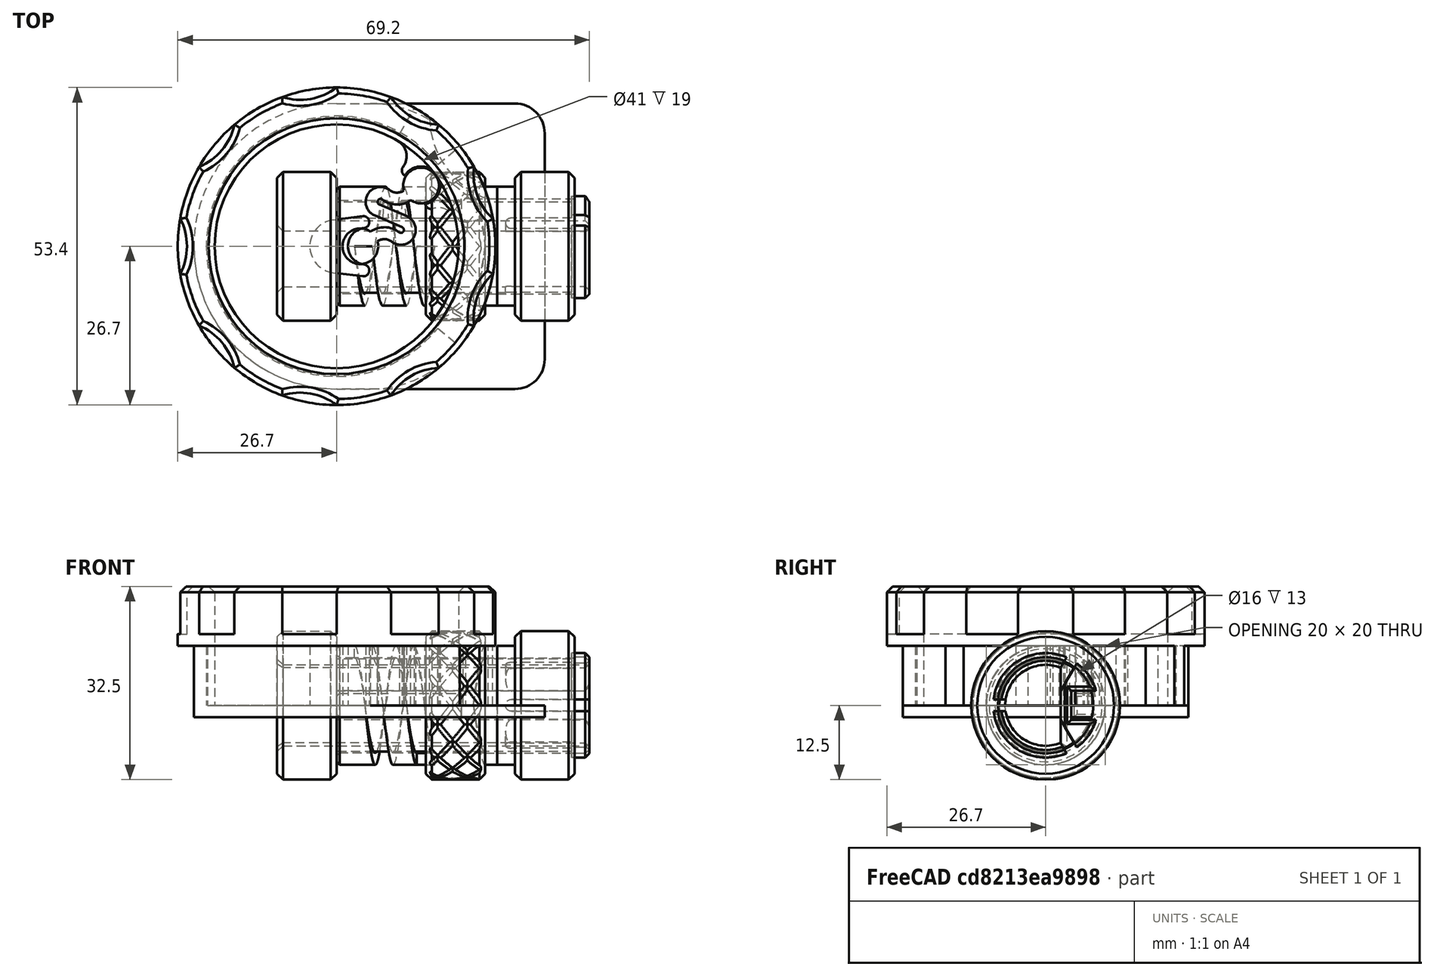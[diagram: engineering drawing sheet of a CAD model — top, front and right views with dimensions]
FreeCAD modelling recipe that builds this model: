
FCSTD DOCUMENT  (FreeCAD 1.1R20260108 (Git shallow))
Label: Compliance rotative switch v0
License: Creative Commons Attribution-NonCommercial-ShareAlike 4.0
LicenseURL: https://creativecommons.org/licenses/by-nc-sa/4.0/
objects: Sketcher::SketchObject×24, PartDesign::Pad×15, PartDesign::SubShapeBinder×13, App::Point×9, PartDesign::Chamfer×7, PartDesign::Body×6, PartDesign::Pocket×5, PartDesign::Mirrored×4, PartDesign::PolarPattern×3, PartDesign::SubtractiveHelix×3, App::Part×3, PartDesign::MultiTransform×2
note: 175 computed .brp shape members not serialized (recipe doc carries the construction recipe); baked Part::Feature solids carry a one-line shape summary decoded from their .brp

FEATURE [App::Point] Origin001  label="Origine"
  Role = Origin
FEATURE [Sketcher::SketchObject] Sketch
  ArcFitTolerance = 1e-06
  AttachmentSupport = -> [Origin]
  ExternalTypes = [0]
  FullyConstrained = true
  MakeInternals = false
  MapMode = 5
  sketch-geometry (19):
    g0: Circle [constr] CenterX=0 CenterY=0 CenterZ=0 NormalX=0 NormalY=0 NormalZ=1 AngleXU=0 Radius=17.5
    g1: ArcOfCircle CenterX=4 CenterY=0 CenterZ=0 NormalX=0 NormalY=0 NormalZ=1 AngleXU=0 Radius=3 StartAngle=0.958197 EndAngle=6.56171
    g2: ArcOfCircle CenterX=14.2117 CenterY=10.2117 CenterZ=0 NormalX=0 NormalY=0 NormalZ=1 AngleXU=0 Radius=3 StartAngle=4.09979 EndAngle=9.7033
    g3: ArcOfCircle CenterX=10.1679 CenterY=11.0165 CenterZ=0 NormalX=0 NormalY=0 NormalZ=1 AngleXU=0 Radius=4 StartAngle=4.04957 EndAngle=5.33075
    g4: LineSegment [constr] StartX=4 StartY=0 StartZ=0 EndX=6.30469 EndY=1.63964 EndZ=0
    g5: LineSegment [constr] StartX=5.72499 StartY=2.45447 StartZ=0 EndX=6.88439 EndY=0.824807 EndZ=0
    g6: LineSegment [constr] StartX=11.3273 StartY=9.38687 StartZ=0 EndX=12.4867 EndY=7.75721 EndZ=0
    g7: LineSegment [constr] StartX=11.907 StartY=8.57204 StartZ=0 EndX=14.2117 EndY=10.2117 EndZ=0
    g8: ArcOfCircle CenterX=10.1679 CenterY=11.0165 CenterZ=0 NormalX=0 NormalY=0 NormalZ=1 AngleXU=0 Radius=2 StartAngle=4.04957 EndAngle=5.33075
    g9: LineSegment [constr] StartX=4 StartY=0 StartZ=0 EndX=14.2117 EndY=10.2117 EndZ=0
    g10: ArcOfCircle CenterX=8.04379 CenterY=-0.804853 CenterZ=0 NormalX=0 NormalY=0 NormalZ=1 AngleXU=0 Radius=2 StartAngle=0.907978 EndAngle=2.18916
    g11: ArcOfCircle CenterX=8.04379 CenterY=-0.804853 CenterZ=0 NormalX=0 NormalY=0 NormalZ=1 AngleXU=0 Radius=4 StartAngle=0.907978 EndAngle=2.18916
    g12: Circle [constr] CenterX=9.10584 CenterY=5.10584 CenterZ=0 NormalX=0 NormalY=0 NormalZ=1 AngleXU=0 Radius=1
    g13: LineSegment StartX=6.41406 StartY=5.17149 StartZ=0 EndX=11.0098 EndY=3.20189 EndZ=0
    g14: LineSegment StartX=7.20189 StartY=7.00978 StartZ=0 EndX=11.7976 EndY=5.04018 EndZ=0
    g15: ArcOfCircle CenterX=10.8128 CenterY=2.74232 CenterZ=0 NormalX=0 NormalY=0 NormalZ=1 AngleXU=0 Radius=0.5 StartAngle=4.04957 EndAngle=7.44909
    g16: ArcOfCircle CenterX=10.8128 CenterY=2.74232 CenterZ=0 NormalX=0 NormalY=0 NormalZ=1 AngleXU=0 Radius=2.5 StartAngle=4.04957 EndAngle=7.44909
    g17: ArcOfCircle CenterX=7.39885 CenterY=7.46935 CenterZ=0 NormalX=0 NormalY=0 NormalZ=1 AngleXU=0 Radius=0.5 StartAngle=0.907978 EndAngle=4.3075
    g18: ArcOfCircle CenterX=7.39885 CenterY=7.46935 CenterZ=0 NormalX=0 NormalY=0 NormalZ=1 AngleXU=0 Radius=2.5 StartAngle=0.907978 EndAngle=4.3075
  constraints (49):
    c: Coincident(g0,g-1)
    c: Equal(g1,g2)
    c: Radius(g2) = 3
    c: Diameter(g0) = 35
    c: Coincident(g3,g2)
    c: Coincident(g5,g1)
    c: Coincident(g5,g1)
    c: Perpendicular(g4,g5)
    c: Coincident(g6,g2)
    c: Coincident(g6,g2)
    c: Symmetric(g6,g6,g7)
    c: Coincident(g7,g2)
    c: Perpendicular(g3,g6)
    c: Coincident(g8,g2)
    c: Distance(g5,g5) = 2
    c: Coincident(g9,g2)
    c: PointOnObject(g4,g5)
    c: Coincident(g10,g1)
    c: Coincident(g11,g10)
    c: Coincident(g11,g1)
    c: Perpendicular(g10,g5)
    c: Coincident(g3,g8)
    c: Symmetric(g9,g9,g12)
    c: Coincident(g9,g1)
    c: Coincident(g1,g4)
    c: Radius(g10) = 2
    c: Equal(g3,g11)
    c: Distance(g1,g0) = 4
    c: PointOnObject(g2,g0)
    c: PointOnObject(g1,g-1)
    c: Angle(g-1,g9) = 0.785398
    c: Tangent(g13,g12)
    c: Tangent(g14,g12)
    c: Coincident(g15,g13)
    c: Coincident(g16,g15)
    c: Coincident(g18,g17)
    c: Tangent(g13,g15,g13) = 1.5708
    c: Tangent(g15,g11) = 1.5708
    c: Tangent(g16,g10) = 1.5708
    c: Tangent(g18,g13) = -1.5708
    c: Tangent(g17,g14) = -1.5708
    c: Tangent(g17,g3) = 1.5708
    c: Tangent(g18,g8) = 1.5708
    c: Tangent(g16,g14) = 1.5708
    c: Equal(g16,g18)
    c: Equal(g17,g15)
    c: Radius(g15) = 0.5
    c: Symmetric(g13,g14,g9)
    c: Distance(g13,g13) = 5
FEATURE [App::Point] Origin003  label="Origine002"
  Role = Origin
FEATURE [PartDesign::SubShapeBinder] Binder
  BindCopyOnChange = 0
  BindMode = 0
  ClaimChildren = false
  Context = -> Body001 [Binder.]
  Fuse = false
  MakeFace = true
  OffsetFill = false
  OffsetIntersection = false
  OffsetJoinType = 0
  OffsetOpenResult = false
  PartialLoad = false
  Refine = true
  Relative = true
  Support = -> [Body[Sketch.Edge1]]
  _Version = 2
FEATURE [PartDesign::SubShapeBinder] Binder001
  BindCopyOnChange = 0
  BindMode = 0
  ClaimChildren = false
  Context = -> Body001 [Binder001.]
  Fuse = false
  MakeFace = true
  OffsetFill = false
  OffsetIntersection = false
  OffsetJoinType = 0
  OffsetOpenResult = false
  PartialLoad = false
  Refine = true
  Relative = true
  Support = -> [Body[Pad.]]
  _Version = 2
FEATURE [Sketcher::SketchObject] Sketch001
  ArcFitTolerance = 1e-06
  AttachmentSupport = -> [Origin002]
  ExternalTypes = [0,0]
  FullyConstrained = false
  MakeInternals = false
  MapMode = 5
  sketch-geometry (10):
    g0: Circle CenterX=0 CenterY=0 CenterZ=0 NormalX=0 NormalY=0 NormalZ=1 AngleXU=0 Radius=21.7
    g1: ArcOfCircle CenterX=0 CenterY=0 CenterZ=0 NormalX=0 NormalY=0 NormalZ=1 AngleXU=0 Radius=20.5 StartAngle=1.04586 EndAngle=6.48345
    g2: ArcOfCircle CenterX=15.9013 CenterY=7.30734 CenterZ=0 NormalX=0 NormalY=0 NormalZ=1 AngleXU=0 Radius=1.02476 StartAngle=3.35859 EndAngle=5.0279
    g3: LineSegment [constr] StartX=14.9006 StartY=7.08672 StartZ=0 EndX=14.2117 EndY=10.2117 EndZ=0
    g4: ArcOfCircle CenterX=11.9981 CenterY=12.7395 CenterZ=0 NormalX=0 NormalY=0 NormalZ=1 AngleXU=0 Radius=1.02476 StartAngle=2.50141 EndAngle=4.17072
    g5: ArcOfCircle CenterX=8.77029 CenterY=15.1437 CenterZ=0 NormalX=0 NormalY=0 NormalZ=1 AngleXU=0 Radius=3 StartAngle=5.643 EndAngle=7.32904
    g6: LineSegment [constr] StartX=11.4698 StartY=11.8615 StartZ=0 EndX=14.2117 EndY=10.2117 EndZ=0
    g7: LineSegment [constr] StartX=13.1691 StartY=9.46257 StartZ=0 EndX=0 EndY=0 EndZ=0
    g8: ArcOfCircle CenterX=17.1502 CenterY=3.48126 CenterZ=0 NormalX=0 NormalY=0 NormalZ=1 AngleXU=0 Radius=3 StartAngle=0.200265 EndAngle=1.88631
    g9: ArcOfCircle CenterX=14.2117 CenterY=10.2117 CenterZ=0 NormalX=0 NormalY=0 NormalZ=1 AngleXU=0 Radius=3.2 StartAngle=4.92938 EndAngle=8.88311
  constraints (23):
    c: Coincident(g0,g-1)
    c: Coincident(g1,g0)
    c: Tangent(g1,g-3)
    c: Distance(g1,g0) = 1.2
    c: Distance(g2,g-4) = 1
    c: Coincident(g3,g-3)
    c: Tangent(g3,g2) = 1.5708
    c: Equal(g2,g4)
    c: Tangent(g5,g4) = 1.5708
    c: Tangent(g5,g1) = -1.5708
    c: Coincident(g6,g3)
    c: Tangent(g6,g4) = -1.5708
    c: Coincident(g7,g0)
    c: Symmetric(g2,g4,g7)
    c: Tangent(g8,g1) = -1.5708
    c: Tangent(g8,g2) = 1.5708
    c: Equal(g8,g5)
    c: PointOnObject(g8,g-4)
    c: PointOnObject(g4,g-4)
    c: Coincident(g9,g3)
    c: Distance(g9,g-3) = 0.2
    c: Coincident(g9,g2)
    c: Coincident(g9,g4)
FEATURE [PartDesign::Pad] Pad001
  Direction = (0,0,1)
  Length = 10
  Length2 = 10
  Profile = -> Sketch001
  ReferenceAxis = -> Sketch001 [N_Axis]
  Refine = true
  SideType = 0
  Suppressed = false
  Type = 0
  Type2 = 0
FEATURE [App::Point] Origin005  label="Origine004"
  Role = Origin
FEATURE [PartDesign::SubShapeBinder] Binder002
  BindCopyOnChange = 0
  BindMode = 0
  ClaimChildren = false
  Context = -> Body002 [Binder002.]
  Fuse = false
  MakeFace = true
  OffsetFill = false
  OffsetIntersection = false
  OffsetJoinType = 0
  OffsetOpenResult = false
  PartialLoad = false
  Refine = true
  Relative = true
  Support = -> [Body001]
  _Version = 2
FEATURE [PartDesign::SubShapeBinder] Binder003
  BindCopyOnChange = 0
  BindMode = 0
  ClaimChildren = false
  Context = -> Body002 [Binder003.]
  Fuse = false
  MakeFace = true
  OffsetFill = false
  OffsetIntersection = false
  OffsetJoinType = 0
  OffsetOpenResult = false
  PartialLoad = false
  Refine = true
  Relative = true
  Support = -> [Body]
  _Version = 2
FEATURE [Sketcher::SketchObject] Sketch002  label="Master"
  ArcFitTolerance = 1e-06
  AttachmentSupport = -> [Origin004]
  ExternalTypes = [0,0,0]
  FullyConstrained = true
  MakeInternals = false
  MapMode = 5
  sketch-geometry (13):
    g0: LineSegment StartX=1.5e-15 StartY=24 StartZ=0 EndX=30 EndY=24 EndZ=0
    g1: LineSegment StartX=35 StartY=19 StartZ=0 EndX=35 EndY=-19 EndZ=0
    g2: LineSegment StartX=30 StartY=-24 StartZ=0 EndX=-3.6e-15 EndY=-24 EndZ=0
    g3: ArcOfCircle CenterX=0 CenterY=0 CenterZ=0 NormalX=0 NormalY=0 NormalZ=1 AngleXU=0 Radius=24 StartAngle=1.5708 EndAngle=4.71239
    g4: ArcOfCircle CenterX=4 CenterY=0 CenterZ=0 NormalX=0 NormalY=0 NormalZ=1 AngleXU=0 Radius=5.2 StartAngle=1.8112 EndAngle=4.47198
    g5: ArcOfCircle CenterX=3 CenterY=4.07922 CenterZ=0 NormalX=0 NormalY=0 NormalZ=1 AngleXU=0 Radius=1 StartAngle=4.95279 EndAngle=8.09439
    g6: ArcOfCircle CenterX=3 CenterY=-4.07922 CenterZ=0 NormalX=0 NormalY=0 NormalZ=1 AngleXU=0 Radius=1 StartAngle=4.47198 EndAngle=7.61358
    g7: ArcOfCircle CenterX=4 CenterY=0 CenterZ=0 NormalX=0 NormalY=0 NormalZ=1 AngleXU=0 Radius=3.2 StartAngle=1.8112 EndAngle=4.47198
    g8: ArcOfCircle CenterX=30 CenterY=19 CenterZ=0 NormalX=0 NormalY=0 NormalZ=1 AngleXU=0 Radius=5 StartAngle=0 EndAngle=1.5708
    g9: GeomPoint [constr] X=35 Y=24 Z=0
    g10: ArcOfCircle CenterX=30 CenterY=-19 CenterZ=0 NormalX=0 NormalY=0 NormalZ=1 AngleXU=0 Radius=5 StartAngle=4.71239 EndAngle=6.28319
    g11: GeomPoint [constr] X=35 Y=-24 Z=0
    g12: LineSegment [constr] StartX=4 StartY=4.07922 StartZ=0 EndX=4 EndY=-4.07922 EndZ=0
  constraints (32):
    c: PointOnObject(g0,g-2)
    c: Horizontal(g0)
    c: Vertical(g1)
    c: PointOnObject(g2,g-2)
    c: Tangent(g2,g3) = 1.5708
    c: Coincident(g3,g0)
    c: Coincident(g3,g-1)
    c: Radius(g3) = 24
    c: Coincident(g4,g7)
    c: Tangent(g7,g6) = 1.5708
    c: Tangent(g7,g5) = 1.5708
    c: Tangent(g4,g6) = -1.5708
    c: Tangent(g4,g5) = -1.5708
    c: Radius(g6) = 1
    c: Coincident(g4,g-4)
    c: Distance(g6,g-4) = 0.2
    c: Vertical(g6,g5)
    c: DistanceX(g2,g11) = 35
    c: PointOnObject(g9,g0)
    c: PointOnObject(g9,g1)
    c: Tangent(g0,g8) = 1.5708
    c: Tangent(g1,g8) = 1.5708
    c: PointOnObject(g11,g2)
    c: PointOnObject(g11,g1)
    c: Tangent(g2,g10) = 1.5708
    c: Tangent(g1,g10) = 1.5708
    c: Equal(g10,g8)
    c: Radius(g8) = 5
    c: PointOnObject(g12,g5)
    c: Tangent(g12,g6) = 1.5708
    c: Vertical(g12)
    c: PointOnObject(g4,g12)
FEATURE [Sketcher::SketchObject] Sketch004
  ArcFitTolerance = 1e-06
  AttachmentSupport = -> [Origin002]
  ExternalGeometry = -> [Pad001]
  ExternalTypes = [0,0]
  FullyConstrained = true
  MakeInternals = false
  MapMode = 5
  sketch-geometry (7):
    g0: LineSegment StartX=21.3184 StartY=4.05156 StartZ=0 EndX=26.2305 EndY=4.9851 EndZ=0
    g1: LineSegment StartX=10.6404 StartY=18.9122 StartZ=0 EndX=13.0921 EndY=23.2698 EndZ=0
    g2: ArcOfCircle CenterX=0 CenterY=0 CenterZ=0 NormalX=0 NormalY=0 NormalZ=1 AngleXU=0 Radius=26.7 StartAngle=0.18781 EndAngle=0.300229
    g3: ArcOfCircle CenterX=30.616 CenterY=21.9989 CenterZ=0 NormalX=0 NormalY=0 NormalZ=1 AngleXU=0 Radius=15 StartAngle=3.16457 EndAngle=4.36474
    g4: ArcOfCircle CenterX=0 CenterY=0 CenterZ=0 NormalX=0 NormalY=0 NormalZ=1 AngleXU=0 Radius=26.7 StartAngle=0.945895 EndAngle=1.05831
    g5: ArcOfCircle CenterX=0 CenterY=0 CenterZ=0 NormalX=0 NormalY=0 NormalZ=1 AngleXU=0 Radius=21.7 StartAngle=0.18781 EndAngle=1.05831
    g6: LineSegment [constr] StartX=0 StartY=0 StartZ=0 EndX=18.4346 EndY=13.246 EndZ=0
  constraints (21):
    c: PointOnObject(g-1,g1)
    c: Distance(g1,g1) = 5
    c: PointOnObject(g-1,g0)
    c: Coincident(g2,g-1)
    c: Coincident(g4,g1)
    c: Coincident(g2,g0)
    c: Radius(g3) = 15
    c: Distance(g3,g-4) = 1
    c: Coincident(g3,g4)
    c: Coincident(g3,g2)
    c: Coincident(g2,g4)
    c: Coincident(g0,g5)
    c: Coincident(g5,g2)
    c: Coincident(g1,g5)
    c: PointOnObject(g1,g-4)
    c: Coincident(g6,g2)
    c: Symmetric(g0,g1,g6)
    c: PointOnObject(g3,g6)
    c: PointOnObject(g-3,g6)
    c: Distance(g0,g2) = 3
    c: PointOnObject(g6,g3)
FEATURE [PartDesign::Pad] Pad005
  BaseFeature = -> Pad001
  Direction = (0,0,1)
  Length = 15
  Length2 = -5
  Profile = -> Sketch004
  ReferenceAxis = -> Sketch004 [N_Axis]
  Refine = true
  SideType = 0
  Suppressed = false
  Type = 3
  Type2 = 0
  UpToFace = -> Pad001 [Face9]
FEATURE [Sketcher::SketchObject] Sketch005
  ArcFitTolerance = 1e-06
  ExternalGeometry = -> [Binder002]
  ExternalTypes = [0,0]
  FullyConstrained = true
  MakeInternals = false
  MapMode = 5
  sketch-geometry (7):
    g0: LineSegment StartX=1.5e-15 StartY=24 StartZ=0 EndX=5.66707 EndY=24 EndZ=0
    g1: ArcOfCircle CenterX=0 CenterY=0 CenterZ=0 NormalX=0 NormalY=0 NormalZ=1 AngleXU=0 Radius=24 StartAngle=1.5708 EndAngle=3.14159
    g2: LineSegment StartX=-24 StartY=2.9e-15 StartZ=0 EndX=-21.9 EndY=2.9e-15 EndZ=0
    g3: ArcOfCircle CenterX=0 CenterY=0 CenterZ=0 NormalX=0 NormalY=0 NormalZ=1 AngleXU=0 Radius=21.9 StartAngle=0.681557 EndAngle=3.14159
    g4: LineSegment StartX=17.0074 StartY=13.7971 StartZ=0 EndX=20.735 EndY=16.8211 EndZ=0
    g5: ArcOfCircle CenterX=5.66707 CenterY=4.59734 CenterZ=0 NormalX=0 NormalY=0 NormalZ=1 AngleXU=0 Radius=19.4027 StartAngle=0.681558 EndAngle=1.5708
    g6: ArcOfCircle [constr] CenterX=0 CenterY=0 CenterZ=0 NormalX=0 NormalY=0 NormalZ=1 AngleXU=0 Radius=26.7 StartAngle=0.681557 EndAngle=1.05831
  constraints (19):
    c: PointOnObject(g0,g-6)
    c: Coincident(g1,g-6)
    c: PointOnObject(g1,g-1)
    c: Coincident(g2,g1)
    c: Horizontal(g2)
    c: Coincident(g-6,g0)
    c: Coincident(g1,g-3)
    c: Coincident(g3,g1)
    c: Coincident(g3,g2)
    c: Distance(g2,g-7) = 0.2
    c: Coincident(g4,g3)
    c: PointOnObject(g1,g4)
    c: Distance(g-8,g4) = 10
    c: Coincident(g5,g4)
    c: Tangent(g5,g0) = 1.5708
    c: Coincident(g6,g1)
    c: Coincident(g6,g-8)
    c: Coincident(g6,g4)
    c: Tangent(g6,g5)
FEATURE [Sketcher::SketchObject] Sketch006
  ArcFitTolerance = 1e-06
  AttachmentSupport = -> [Pad005]
  ExternalGeometry = -> [Pad005]
  ExternalTypes = [0,0]
  FullyConstrained = true
  MakeInternals = false
  MapMode = 5
  Placement = pos=(0,0,10) rot=(0,0,1;0rad)
  sketch-geometry (2):
    g0: Circle CenterX=0 CenterY=0 CenterZ=0 NormalX=0 NormalY=0 NormalZ=1 AngleXU=0 Radius=20.5
    g1: Circle CenterX=0 CenterY=0 CenterZ=0 NormalX=0 NormalY=0 NormalZ=1 AngleXU=0 Radius=26.7
  constraints (4):
    c: Coincident(g0,g-1)
    c: PointOnObject(g-4,g0)
    c: Coincident(g1,g0)
    c: PointOnObject(g-3,g1)
FEATURE [PartDesign::Pad] Pad007
  BaseFeature = -> Pad005
  Direction = (0,0,1)
  Length = 10
  Length2 = 10
  Profile = -> Sketch006
  ReferenceAxis = -> Sketch006 [N_Axis]
  Refine = true
  SideType = 0
  Suppressed = false
  Type = 0
  Type2 = 0
FEATURE [Sketcher::SketchObject] Sketch007
  ArcFitTolerance = 1e-06
  AttachmentSupport = -> [Pad007]
  ExternalGeometry = -> [Pad007]
  ExternalTypes = [0]
  FullyConstrained = false
  MakeInternals = false
  MapMode = 5
  Placement = pos=(0,0,20) rot=(0,0,1;0rad)
  sketch-geometry (5):
    g0: ArcOfCircle CenterX=-35.1546 CenterY=1.9e-15 CenterZ=0 NormalX=0 NormalY=0 NormalZ=1 AngleXU=0 Radius=10 StartAngle=5.80109 EndAngle=6.76529
    g1: LineSegment [constr] StartX=-26.2944 StartY=4.63641 StartZ=0 EndX=0 EndY=0 EndZ=0
    g2: LineSegment [constr] StartX=-26.2944 StartY=-4.63641 StartZ=0 EndX=0 EndY=0 EndZ=0
    g3: LineSegment [constr] StartX=-26.2944 StartY=4.63641 StartZ=0 EndX=-26.2944 EndY=-4.63641 EndZ=0
    g4: ArcOfCircle CenterX=0 CenterY=0 CenterZ=0 NormalX=0 NormalY=0 NormalZ=1 AngleXU=0 Radius=26.7 StartAngle=2.96706 EndAngle=3.31613
  constraints (13):
    c: Symmetric(g0,g0,g-1)
    c: Coincident(g1,g0)
    c: Coincident(g1,g-1)
    c: Coincident(g2,g0)
    c: Radius(g0) = 10
    c: Coincident(g2,g1)
    c: Coincident(g3,g0)
    c: Coincident(g3,g0)
    c: Coincident(g4,g0)
    c: Coincident(g4,g1)
    c: PointOnObject(g4,g-3)
    c: Horizontal(g0,g4)
    c: Angle(g1,g2) = 0.349066
FEATURE [PartDesign::Pocket] Pocket
  BaseFeature = -> Pad007
  Direction = (0,0,-1)
  Length = 8
  Length2 = 5
  Profile = -> Sketch007
  ReferenceAxis = -> Sketch007 [N_Axis]
  Refine = true
  SideType = 0
  Suppressed = false
  Type = 0
  Type2 = 0
FEATURE [PartDesign::PolarPattern] PolarPattern
  Angle = 360
  Axis = -> Sketch007 [N_Axis]
  BaseFeature = -> Pocket
  Mode = 0
  Occurrences = 9
  Offset = 120
  Originals = -> [Pocket]
  Refine = true
  SpacingPattern = [0]
  Spacings = [-1,-1,-1,-1,-1,-1,-1,-1]
  Suppressed = false
  TransformMode = 0
FEATURE [PartDesign::Chamfer] Chamfer
  Angle = 45
  Base = -> PolarPattern [Face14]
  BaseFeature = -> PolarPattern
  ChamferType = 0
  FlipDirection = false
  Refine = true
  Size = 1
  Size2 = 1
  SupportTransform = false
  Suppressed = false
  UseAllEdges = false
FEATURE [PartDesign::Body] Body001  label="Bouton"
  AllowCompound = false
  Group = -> [Binder,Binder001,Sketch001,Pad001,Sketch004,Pad005,Pad007,Pocket,Sketch006,Sketch007,PolarPattern,Chamfer]
  Origin = -> Origin002
  Tip = -> Chamfer
FEATURE [Sketcher::SketchObject] Sketch008
  ArcFitTolerance = 1e-06
  AttachmentSupport = -> [Origin004]
  ExternalGeometry = -> [Sketch002]
  ExternalTypes = [0,0,0,0,0,0]
  FullyConstrained = true
  MakeInternals = false
  MapMode = 5
FEATURE [PartDesign::Pad] Pad008  label="Plaque"
  Direction = (0,0,1)
  Length = 2
  Length2 = 10
  Profile = -> Sketch008
  ReferenceAxis = -> Sketch008 [N_Axis]
  Refine = true
  Reversed = true
  SideType = 0
  Suppressed = false
  Type = 0
  Type2 = 0
FEATURE [Sketcher::SketchObject] Sketch009  label="Axis"
  ArcFitTolerance = 1e-06
  AttachmentSupport = -> [Origin004]
  ExternalGeometry = -> [Sketch002]
  ExternalTypes = [0,0,0,0]
  FullyConstrained = true
  MakeInternals = false
  MapMode = 5
  sketch-geometry (7):
    g0: ArcOfCircle [constr] CenterX=5 CenterY=0 CenterZ=0 NormalX=0 NormalY=0 NormalZ=1 AngleXU=0 Radius=5.08839 StartAngle=1.69297 EndAngle=4.59022
    g1: ArcOfCircle CenterX=4.50175 CenterY=4.05791 CenterZ=0 NormalX=0 NormalY=0 NormalZ=1 AngleXU=0 Radius=1 StartAngle=4.83456 EndAngle=7.97615
    g2: ArcOfCircle CenterX=4.50175 CenterY=-4.05791 CenterZ=0 NormalX=0 NormalY=0 NormalZ=1 AngleXU=0 Radius=1 StartAngle=4.59022 EndAngle=7.73181
    g3: ArcOfCircle CenterX=5 CenterY=0 CenterZ=0 NormalX=0 NormalY=0 NormalZ=1 AngleXU=0 Radius=3.08839 StartAngle=1.69297 EndAngle=4.59022
    g4: ArcOfCircle CenterX=0 CenterY=0 CenterZ=0 NormalX=0 NormalY=0 NormalZ=1 AngleXU=0 Radius=4.47904 StartAngle=1.69297 EndAngle=4.59022
    g5: LineSegment StartX=-0.545858 StartY=4.44565 StartZ=0 EndX=4.37988 EndY=5.05046 EndZ=0
    g6: LineSegment StartX=-0.545858 StartY=-4.44565 StartZ=0 EndX=4.37988 EndY=-5.05046 EndZ=0
  constraints (16):
    c: Coincident(g0,g3)
    c: Tangent(g3,g2) = 1.5708
    c: Tangent(g3,g1) = 1.5708
    c: Tangent(g0,g2) = -1.5708
    c: Tangent(g0,g1) = -1.5708
    c: PointOnObject(g0,g-1)
    c: Equal(g1,g-4)
    c: Distance(g-5,g0) = 1
    c: Horizontal(g0,g-4)
    c: Vertical(g2,g1)
    c: Tangent(g5,g0) = 1.5708
    c: Coincident(g6,g0)
    c: Tangent(g5,g4) = 1.5708
    c: Tangent(g6,g4) = -1.5708
    c: Coincident(g4,g-1)
    c: Angle(g-1,g5) = 0.122173
FEATURE [PartDesign::Pad] Pad009  label="Axe"
  BaseFeature = -> Pad008
  Direction = (0,0,1)
  Length = 10
  Length2 = 10
  Profile = -> Sketch009
  ReferenceAxis = -> Sketch009 [N_Axis]
  Refine = true
  SideType = 0
  Suppressed = false
  Type = 3
  Type2 = 0
  UpToFace = -> Binder003 [Face14]
FEATURE [PartDesign::Pad] Pad006
  BaseFeature = -> Pad009
  Direction = (0,0,1)
  Length = 10
  Length2 = 10
  Profile = -> Sketch005
  ReferenceAxis = -> Sketch005 [N_Axis]
  Refine = true
  SideType = 0
  Suppressed = false
  Type = 3
  Type2 = 0
  UpToFace = -> Binder002 [Face3]
FEATURE [PartDesign::Mirrored] Mirrored
  BaseFeature = -> Pad006
  MirrorPlane = -> XZ_Plane002
  Originals = -> [Pad006]
  Refine = true
  Suppressed = false
  TransformMode = 0
FEATURE [PartDesign::Body] Body002  label="Support"
  AllowCompound = false
  Group = -> [Binder003,Binder002,Sketch002,Pad008,Pad009,Sketch005,Pad006,Mirrored,Sketch008,Sketch009]
  Origin = -> Origin004
  Tip = -> Mirrored
FEATURE [PartDesign::Pad] Pad
  Direction = (0,0,1)
  Length = 10
  Length2 = 10
  Profile = -> Sketch
  ReferenceAxis = -> Sketch [N_Axis]
  Refine = true
  SideType = 0
  Suppressed = false
  Type = 0
  Type2 = 0
FEATURE [PartDesign::Body] Body  label="Ressort"
  AllowCompound = false
  Group = -> [Sketch,Pad]
  Origin = -> Origin
  Tip = -> Pad
FEATURE [App::Point] Origin007  label="Origine006"
  Role = Origin
FEATURE [Sketcher::SketchObject] Sketch010
  ArcFitTolerance = 1e-06
  AttachmentSupport = -> [Origin006]
  ExternalTypes = [0]
  FullyConstrained = true
  MakeInternals = false
  MapMode = 5
  Placement = pos=(0,0,0) rot=(0.57735,0.57735,0.57735;2.0944rad)
  sketch-geometry (5):
    g0: Circle CenterX=0 CenterY=0 CenterZ=0 NormalX=0 NormalY=0 NormalZ=1 AngleXU=0 Radius=10
    g1: ArcOfCircle CenterX=0 CenterY=0 CenterZ=0 NormalX=0 NormalY=0 NormalZ=1 AngleXU=0 Radius=8 StartAngle=0.25268 EndAngle=6.03051
    g2: LineSegment StartX=7.74597 StartY=2 StartZ=0 EndX=4.74597 EndY=2 EndZ=0
    g3: LineSegment StartX=4.74597 StartY=2 StartZ=0 EndX=4.74597 EndY=-2 EndZ=0
    g4: LineSegment StartX=4.74597 StartY=-2 StartZ=0 EndX=7.74597 EndY=-2 EndZ=0
  constraints (13):
    c: Diameter(g0) = 20
    c: Coincident(g0,g-1)
    c: Coincident(g1,g0)
    c: Coincident(g2,g3)
    c: Coincident(g3,g4)
    c: Distance(g3,g3) = 4
    c: Distance(g4,g4) = 3
    c: Distance(g0,g1) = 2
    c: Coincident(g2,g1)
    c: Coincident(g4,g1)
    c: Horizontal(g4)
    c: Horizontal(g2)
    c: Symmetric(g2,g3,g-1)
FEATURE [PartDesign::Pad] Pad010
  Direction = (1,0,0)
  Length = 25
  Length2 = 10
  Profile = -> Sketch010
  ReferenceAxis = -> Sketch010 [N_Axis]
  Refine = true
  SideType = 0
  Suppressed = false
  Type = 0
  Type2 = 0
FEATURE [Sketcher::SketchObject] Sketch011
  ArcFitTolerance = 1e-06
  AttachmentSupport = -> [Origin006]
  ExternalGeometry = -> [Pad010]
  ExternalTypes = [1,1]
  FullyConstrained = true
  MakeInternals = false
  MapMode = 5
  Placement = pos=(0,0,0) rot=(1,0,0;1.5708rad)
  sketch-geometry (4):
    g0: LineSegment StartX=6 StartY=10 StartZ=0 EndX=3 EndY=10 EndZ=0
    g1: LineSegment StartX=3 StartY=10 StartZ=0 EndX=3 EndY=0 EndZ=0
    g2: LineSegment StartX=3 StartY=0 StartZ=0 EndX=6 EndY=0 EndZ=0
    g3: LineSegment StartX=6 StartY=0 StartZ=0 EndX=6 EndY=10 EndZ=0
  constraints (12):
    c: Horizontal(g0)
    c: Horizontal(g-5,g0)
    c: DistanceX(g-5,g0) = 3
    c: Coincident(g0,g1)
    c: PointOnObject(g1,g-1)
    c: Vertical(g1)
    c: Coincident(g1,g2)
    c: Horizontal(g2)
    c: Coincident(g2,g3)
    c: Coincident(g3,g0)
    c: Vertical(g3)
    c: Distance(g0,g0) = 3
FEATURE [PartDesign::SubtractiveHelix] SubtractiveHelix
  Angle = 0
  Axis = (1,0,0)
  Base = (0,0,0)
  BaseFeature = -> Pad010
  Growth = 0
  HasBeenEdited = true
  Height = 10.5
  LeftHanded = false
  Mode = 1
  Outside = false
  Pitch = 7
  Profile = -> Sketch011
  ReferenceAxis = -> Sketch011 [H_Axis]
  Refine = true
  Suppressed = false
  Tolerance = 0.1
  Turns = 1.5
FEATURE [App::Point] Origin009  label="Origine008"
  Role = Origin
FEATURE [PartDesign::SubShapeBinder] Binder004
  BindCopyOnChange = 0
  BindMode = 0
  ClaimChildren = false
  Context = -> Part001 [Body004.Binder004.]
  Fuse = false
  MakeFace = true
  OffsetFill = false
  OffsetIntersection = false
  OffsetJoinType = 0
  OffsetOpenResult = false
  PartialLoad = false
  Refine = true
  Relative = true
  Support = -> [Body003]
  _Version = 2
FEATURE [Sketcher::SketchObject] Sketch013
  ArcFitTolerance = 1e-06
  AttachmentOffset = pos=(0,0,40) rot=(0,0,1;0rad)
  AttachmentSupport = -> [Origin008]
  ExternalTypes = [0,0]
  FullyConstrained = true
  MakeInternals = false
  MapMode = 5
  Placement = pos=(40,0,0) rot=(0.57735,0.57735,0.57735;2.0944rad)
  sketch-geometry (2):
    g0: Circle CenterX=0 CenterY=0 CenterZ=0 NormalX=0 NormalY=0 NormalZ=1 AngleXU=0 Radius=10
    g1: Circle CenterX=0 CenterY=0 CenterZ=0 NormalX=0 NormalY=0 NormalZ=1 AngleXU=0 Radius=8
  constraints (4):
    c: Coincident(g0,g-1)
    c: PointOnObject(g-3,g0)
    c: Coincident(g1,g0)
    c: PointOnObject(g-4,g1)
FEATURE [App::Point] Origin011  label="Origine010"
  Role = Origin
FEATURE [PartDesign::SubShapeBinder] Binder005
  BindCopyOnChange = 0
  BindMode = 0
  ClaimChildren = false
  Context = -> Part001 [Body005.Binder005.]
  Fuse = false
  MakeFace = true
  OffsetFill = false
  OffsetIntersection = false
  OffsetJoinType = 0
  OffsetOpenResult = false
  PartialLoad = false
  Refine = true
  Relative = true
  Support = -> [Body003]
  _Version = 2
FEATURE [PartDesign::SubShapeBinder] Binder006
  BindCopyOnChange = 0
  BindMode = 0
  ClaimChildren = false
  Context = -> Part001 [Body005.Binder006.]
  Fuse = false
  MakeFace = true
  OffsetFill = false
  OffsetIntersection = false
  OffsetJoinType = 0
  OffsetOpenResult = false
  PartialLoad = false
  Refine = true
  Relative = true
  Support = -> [Body004]
  _Version = 2
FEATURE [PartDesign::SubShapeBinder] Binder007
  BindCopyOnChange = 0
  BindMode = 0
  ClaimChildren = false
  Context = -> Part001 [Body005.Binder007.]
  Fuse = false
  MakeFace = true
  Offset = 1
  OffsetFill = false
  OffsetIntersection = false
  OffsetJoinType = 2
  OffsetOpenResult = false
  PartialLoad = false
  Refine = true
  Relative = true
  Support = -> [Body003]
  _Version = 2
FEATURE [Sketcher::SketchObject] Sketch015
  ArcFitTolerance = 1e-06
  AttachmentSupport = -> [Origin010]
  ExternalGeometry = -> [Binder007]
  ExternalTypes = [0]
  FullyConstrained = false
  MakeInternals = false
  MapMode = 5
  Placement = pos=(0,0,0) rot=(0.57735,0.57735,0.57735;2.0944rad)
  sketch-geometry (1):
    g0: Circle CenterX=0 CenterY=0 CenterZ=0 NormalX=0 NormalY=0 NormalZ=1 AngleXU=0 Radius=7.8
FEATURE [PartDesign::SubShapeBinder] Binder008
  BindCopyOnChange = 0
  BindMode = 0
  ClaimChildren = false
  Context = -> Part001 [Body003.Binder008.]
  Fuse = false
  MakeFace = true
  OffsetFill = false
  OffsetIntersection = false
  OffsetJoinType = 0
  OffsetOpenResult = false
  PartialLoad = false
  Placement = pos=(1,0,0) rot=(1,0,0;0.785398rad)
  Refine = true
  Relative = true
  Support = -> [Sketch016]
  _Version = 2
FEATURE [PartDesign::SubShapeBinder] Binder009
  BindCopyOnChange = 0
  BindMode = 0
  ClaimChildren = false
  Context = -> Part001 [Body003.Binder009.]
  Fuse = false
  MakeFace = true
  OffsetFill = false
  OffsetIntersection = false
  OffsetJoinType = 0
  OffsetOpenResult = false
  PartialLoad = false
  Placement = pos=(0.99,0,0) rot=(1,0,0;0.733038rad)
  Refine = true
  Relative = true
  Support = -> [Binder008]
  _Version = 2
FEATURE [PartDesign::SubShapeBinder] Binder010
  BindCopyOnChange = 0
  BindMode = 0
  ClaimChildren = false
  Context = -> Part001 [Body003.Binder010.]
  Fuse = false
  MakeFace = true
  OffsetFill = false
  OffsetIntersection = false
  OffsetJoinType = 0
  OffsetOpenResult = false
  PartialLoad = false
  Placement = pos=(0.01,0,0) rot=(1,0,0;0.05236rad)
  Refine = true
  Relative = true
  Support = -> [Sketch016]
  _Version = 2
FEATURE [PartDesign::SubShapeBinder] Binder011
  BindCopyOnChange = 0
  BindMode = 0
  ClaimChildren = false
  Context = -> Part001 [Body003.Binder011.]
  Fuse = false
  MakeFace = true
  OffsetFill = false
  OffsetIntersection = false
  OffsetJoinType = 0
  OffsetOpenResult = false
  PartialLoad = false
  Placement = pos=(0.01,0,0) rot=(1,0,0;0.054105rad)
  Refine = true
  Relative = true
  Support = -> [Binder009]
  _Version = 2
FEATURE [PartDesign::Pad] Pad017
  Direction = (1,0,0)
  Length = 13
  Length2 = 10
  Profile = -> Sketch013
  ReferenceAxis = -> Sketch013 [N_Axis]
  Refine = true
  Reversed = true
  SideType = 0
  Suppressed = false
  Type = 0
  Type2 = 0
  UpToShape = -> [Binder004]
FEATURE [Sketcher::SketchObject] Sketch022
  ArcFitTolerance = 1e-06
  AttachmentOffset = pos=(0,0,0) rot=(1,0,0;0.523599rad)
  AttachmentSupport = -> [Origin010]
  ExternalTypes = [0]
  FullyConstrained = true
  MakeInternals = false
  MapMode = 5
  Placement = pos=(0,0,0) rot=(1,0,0;0.523599rad)
  sketch-geometry (4):
    g0: ArcOfCircle CenterX=44.4 CenterY=1e-16 CenterZ=0 NormalX=0 NormalY=0 NormalZ=1 AngleXU=0 Radius=1 StartAngle=4.71239 EndAngle=7.85398
    g1: ArcOfCircle CenterX=29.4 CenterY=0 CenterZ=0 NormalX=0 NormalY=0 NormalZ=1 AngleXU=0 Radius=1 StartAngle=1.5708 EndAngle=4.71239
    g2: LineSegment StartX=44.4 StartY=-1 StartZ=0 EndX=29.4 EndY=-1 EndZ=0
    g3: LineSegment StartX=44.4 StartY=1 StartZ=0 EndX=29.4 EndY=1 EndZ=0
  constraints (9):
    c: Tangent(g0,g2) = 1.5708
    c: Tangent(g0,g3) = -1.5708
    c: Tangent(g1,g2) = 1.5708
    c: Tangent(g1,g3) = -1.5708
    c: Equal(g0,g1)
    c: Distance(g0,g1) = 15
    c: Radius(g0) = 1
    c: Symmetric(g-3,g-3,g0)
    c: PointOnObject(g1,g-1)
FEATURE [Sketcher::SketchObject] Sketch023
  ArcFitTolerance = 1e-06
  ExternalTypes = [0]
  FullyConstrained = true
  MakeInternals = false
  MapMode = 5
  Placement = pos=(44.4,0,0) rot=(0.57735,0.57735,0.57735;2.0944rad)
  sketch-geometry (1):
    g0: Circle CenterX=0 CenterY=0 CenterZ=0 NormalX=0 NormalY=0 NormalZ=1 AngleXU=0 Radius=6.8
  constraints (2):
    c: Coincident(g0,g-3)
    c: Distance(g0,g-3) = 1.2
FEATURE [Sketcher::SketchObject] Sketch024
  ArcFitTolerance = 1e-06
  AttachmentSupport = -> [Pad017]
  ExternalGeometry = -> [Pad017]
  ExternalTypes = [0]
  FullyConstrained = true
  MakeInternals = false
  MapMode = 5
  Placement = pos=(40,0,0) rot=(0.57735,0.57735,0.57735;2.0944rad)
  sketch-geometry (1):
    g0: Circle CenterX=0 CenterY=0 CenterZ=0 NormalX=0 NormalY=0 NormalZ=1 AngleXU=0 Radius=12.5
  constraints (2):
    c: Diameter(g0) = 25
    c: Coincident(g0,g-3)
FEATURE [PartDesign::Pad] Pad020
  BaseFeature = -> Pad017
  Direction = (1,0,0)
  Length = 10
  Length2 = 10
  Profile = -> Sketch024
  ReferenceAxis = -> Sketch024 [N_Axis]
  Refine = true
  Reversed = true
  SideType = 0
  Suppressed = false
  Type = 0
  Type2 = 0
FEATURE [PartDesign::Chamfer] Chamfer002
  Angle = 45
  Base = -> Pad020 [Face4]
  BaseFeature = -> Pad020
  ChamferType = 0
  FlipDirection = false
  Refine = true
  Size = 1
  Size2 = 1
  SupportTransform = false
  Suppressed = false
  UseAllEdges = false
FEATURE [PartDesign::Chamfer] Chamfer005
  Angle = 45
  Base = -> SubtractiveHelix [Face2]
  BaseFeature = -> SubtractiveHelix
  ChamferType = 0
  FlipDirection = false
  Refine = true
  Size = 0.5
  Size2 = 1
  SupportTransform = false
  Suppressed = false
  UseAllEdges = false
FEATURE [Sketcher::SketchObject] Sketch016
  ArcFitTolerance = 1e-06
  AttachmentSupport = -> [Origin006]
  ExternalGeometry = -> [Chamfer005]
  ExternalTypes = [2]
  FullyConstrained = true
  MakeInternals = false
  MapMode = 5
  sketch-geometry (11):
    g0: LineSegment [constr] StartX=25 StartY=-10 StartZ=0 EndX=23 EndY=-10 EndZ=0
    g1: LineSegment [constr] StartX=23 StartY=-4 StartZ=0 EndX=25 EndY=-4 EndZ=0
    g2: LineSegment [constr] StartX=23 StartY=-4 StartZ=0 EndX=23 EndY=-10 EndZ=0
    g3: LineSegment [constr] StartX=25 StartY=-4 StartZ=0 EndX=25 EndY=-10 EndZ=0
    g4: LineSegment StartX=23 StartY=-2 StartZ=0 EndX=23 EndY=-12 EndZ=0
    g5: LineSegment StartX=23 StartY=-12 StartZ=0 EndX=27 EndY=-12 EndZ=0
    g6: LineSegment StartX=27 StartY=-12 StartZ=0 EndX=27 EndY=-2 EndZ=0
    g7: LineSegment StartX=27 StartY=-2 StartZ=0 EndX=23 EndY=-2 EndZ=0
    g8: ArcOfCircle [constr] CenterX=25 CenterY=-4 CenterZ=0 NormalX=0 NormalY=0 NormalZ=1 AngleXU=0 Radius=2 StartAngle=0 EndAngle=1.5708
    g9: LineSegment [constr] StartX=27 StartY=-2 StartZ=0 EndX=25 EndY=-4 EndZ=0
    g10: LineSegment [constr] StartX=25 StartY=-10 StartZ=0 EndX=27 EndY=-12 EndZ=0
  constraints (29):
    c: Horizontal(g0)
    c: Distance(g0,g0) = 2
    c: Coincident(g2,g1)
    c: Coincident(g2,g0)
    c: Vertical(g2)
    c: Coincident(g3,g1)
    c: Coincident(g3,g0)
    c: Vertical(g3)
    c: Horizontal(g1)
    c: Coincident(g0,g-5)
    c: Distance(g1,g-1) = 4
    c: Coincident(g4,g5)
    c: Coincident(g5,g6)
    c: Coincident(g6,g7)
    c: Coincident(g7,g4)
    c: Vertical(g4)
    c: Vertical(g6)
    c: Horizontal(g5)
    c: Horizontal(g7)
    c: Coincident(g8,g1)
    c: Radius(g8) = 2
    c: Coincident(g9,g6)
    c: Coincident(g9,g1)
    c: Tangent(g8,g7) = -1.5708
    c: Tangent(g8,g6) = -1.5708
    c: PointOnObject(g0,g4)
    c: Coincident(g10,g0)
    c: Coincident(g10,g5)
    c: Equal(g10,g9)
FEATURE [PartDesign::SubtractiveHelix] SubtractiveHelix001
  Angle = 0
  Axis = (1,0,0)
  Base = (0,0,0)
  BaseFeature = -> Chamfer005
  Growth = 0
  HasBeenEdited = true
  Height = 2
  LeftHanded = false
  Mode = 1
  Outside = false
  Pitch = 8
  Profile = -> Sketch016
  ReferenceAxis = -> Sketch016 [H_Axis]
  Refine = true
  Suppressed = false
  Tolerance = 0.1
  Turns = 0.25
FEATURE [PartDesign::Mirrored] Mirror
  MirrorPlane = -> XY_Plane003
  Refine = true
  Suppressed = false
  TransformMode = 0
FEATURE [PartDesign::Mirrored] Mirror001
  MirrorPlane = -> XZ_Plane003
  Refine = true
  Suppressed = false
  TransformMode = 0
FEATURE [PartDesign::MultiTransform] MultiTransform
  BaseFeature = -> SubtractiveHelix001
  Originals = -> [SubtractiveHelix001]
  Refine = true
  Suppressed = false
  TransformMode = 0
  Transformations = -> [Mirror,Mirror001]
FEATURE [Sketcher::SketchObject] Sketch025
  ArcFitTolerance = 1e-06
  AttachmentOffset = pos=(0,0,15) rot=(0,0,1;0rad)
  AttachmentSupport = -> [Origin006]
  ExternalGeometry = -> [MultiTransform]
  ExternalTypes = [0]
  FullyConstrained = true
  MakeInternals = false
  MapMode = 5
  Placement = pos=(15,0,0) rot=(0.57735,0.57735,0.57735;2.0944rad)
  sketch-geometry (2):
    g0: Circle CenterX=0 CenterY=0 CenterZ=0 NormalX=0 NormalY=0 NormalZ=1 AngleXU=0 Radius=12.5
    g1: Circle CenterX=0 CenterY=0 CenterZ=0 NormalX=0 NormalY=0 NormalZ=1 AngleXU=0 Radius=10
  constraints (4):
    c: Diameter(g0) = 25
    c: Coincident(g0,g-1)
    c: Coincident(g1,g0)
    c: PointOnObject(g-3,g1)
FEATURE [PartDesign::Pad] Pad021
  BaseFeature = -> MultiTransform
  Direction = (1,0,0)
  Length = 10
  Length2 = 10
  Profile = -> Sketch025
  ReferenceAxis = -> Sketch025 [N_Axis]
  Refine = true
  SideType = 0
  Suppressed = false
  Type = 0
  Type2 = 0
FEATURE [PartDesign::Chamfer] Chamfer003
  Angle = 45
  Base = -> Pad021 [Face19]
  BaseFeature = -> Pad021
  ChamferType = 0
  FlipDirection = false
  Refine = true
  Size = 1
  Size2 = 1
  SupportTransform = false
  Suppressed = false
  UseAllEdges = false
FEATURE [Sketcher::SketchObject] Sketch026
  ArcFitTolerance = 1e-06
  AttachmentSupport = -> [Origin006]
  ExternalGeometry = -> [Pad010]
  ExternalTypes = [0]
  FullyConstrained = true
  MakeInternals = false
  MapMode = 5
  Placement = pos=(0,0,0) rot=(0.57735,0.57735,0.57735;2.0944rad)
  sketch-geometry (1):
    g0: Circle CenterX=0 CenterY=0 CenterZ=0 NormalX=0 NormalY=0 NormalZ=1 AngleXU=0 Radius=8
  constraints (2):
    c: PointOnObject(g-4,g0)
    c: Coincident(g0,g-4)
FEATURE [PartDesign::Pocket] Pocket007
  BaseFeature = -> Chamfer003
  Direction = (-1,0,0)
  Length = 5
  Length2 = 30
  Offset = -4
  Profile = -> Sketch026
  ReferenceAxis = -> Sketch026 [N_Axis]
  Refine = true
  SideType = 1
  Suppressed = false
  Type = 3
  Type2 = 0
  UpToFace = -> Chamfer003 [Face23]
FEATURE [PartDesign::Pad] Pad023
  Direction = (1,0,0)
  Length = 10
  Length2 = 10
  Offset = -0.5
  Profile = -> Sketch015
  ReferenceAxis = -> Sketch015 [N_Axis]
  Refine = true
  Reversed = true
  SideType = 0
  Suppressed = false
  Type = 3
  Type2 = 0
  UpToFace = -> Binder006 [Face20]
FEATURE [Sketcher::SketchObject] Sketch027
  ArcFitTolerance = 1e-06
  AttachmentSupport = -> [Pad023]
  ExternalGeometry = -> [Binder006]
  ExternalTypes = [0]
  FullyConstrained = true
  MakeInternals = false
  MapMode = 5
  Placement = pos=(0,0,0) rot=(0.57735,-0.57735,-0.57735;2.0944rad)
FEATURE [PartDesign::Pad] Pad024
  BaseFeature = -> Pad023
  Direction = (-1,0,0)
  Length = 10
  Length2 = 10
  Profile = -> Sketch027
  ReferenceAxis = -> Sketch027 [N_Axis]
  Refine = true
  SideType = 0
  Suppressed = false
  Type = 0
  Type2 = 0
FEATURE [PartDesign::Chamfer] Chamfer006
  Angle = 45
  Base = -> Pad024 [Face4]
  BaseFeature = -> Pad024
  ChamferType = 0
  FlipDirection = false
  Refine = true
  Size = 1
  Size2 = 1
  SupportTransform = false
  Suppressed = false
  UseAllEdges = false
FEATURE [Sketcher::SketchObject] Sketch029
  ArcFitTolerance = 1e-06
  ExternalTypes = [0,0]
  FullyConstrained = true
  MakeInternals = false
  MapMode = 5
  Placement = pos=(43.5,0,0) rot=(0.57735,0.57735,0.57735;2.0944rad)
  sketch-geometry (4):
    g0: ArcOfCircle CenterX=0 CenterY=0 CenterZ=0 NormalX=0 NormalY=0 NormalZ=1 AngleXU=0 Radius=6.8 StartAngle=1.18704 EndAngle=5.09615
    g1: LineSegment StartX=2.54597 StartY=6.3054 StartZ=0 EndX=2.54597 EndY=-6.3054 EndZ=0
    g2: LineSegment [constr] StartX=3.74597 StartY=3 StartZ=0 EndX=2.54597 EndY=3 EndZ=0
    g3: LineSegment [constr] StartX=0 StartY=6.8 StartZ=0 EndX=0 EndY=8 EndZ=0
  constraints (13):
    c: Coincident(g0,g-1)
    c: Coincident(g1,g0)
    c: Coincident(g1,g0)
    c: Vertical(g1)
    c: Coincident(g2,g-3)
    c: PointOnObject(g2,g1)
    c: Horizontal(g2)
    c: PointOnObject(g3,g0)
    c: PointOnObject(g3,g-4)
    c: Vertical(g3)
    c: Equal(g2,g3)
    c: PointOnObject(g3,g-2)
    c: Distance(g2,g2) = 1.2
FEATURE [Sketcher::SketchObject] Sketch030
  ArcFitTolerance = 1e-06
  AttachmentSupport = -> [Origin006]
  ExternalGeometry = -> [Pocket007]
  ExternalTypes = [0,0]
  FullyConstrained = true
  MakeInternals = false
  MapMode = 5
  Placement = pos=(0,0,0) rot=(1,0,0;1.5708rad)
  sketch-geometry (2):
    g0: LineSegment StartX=15 StartY=12.5 StartZ=0 EndX=14 EndY=12.5 EndZ=0
    g1: ArcOfCircle CenterX=14.5 CenterY=12.8 CenterZ=0 NormalX=0 NormalY=0 NormalZ=1 AngleXU=0 Radius=0.583095 StartAngle=3.68201 EndAngle=5.74277
  constraints (7):
    c: Distance(g0) = 1
    c: Horizontal(g0)
    c: Vertical(g0,g-11)
    c: Horizontal(g0,g-7)
    c: Coincident(g1,g0)
    c: Coincident(g1,g0)
    c: Distance(g1,g0) = 0.3
FEATURE [PartDesign::SubtractiveHelix] SubtractiveHelix002
  Angle = 0
  Axis = (1,0,0)
  Base = (0,0,0)
  BaseFeature = -> Pocket007
  Growth = 0
  HasBeenEdited = true
  Height = 11
  LeftHanded = false
  Mode = 0
  Outside = false
  Pitch = 60
  Profile = -> Sketch030
  ReferenceAxis = -> X_Axis003
  Refine = true
  Suppressed = false
  Tolerance = 0.1
  Turns = 0.183333
FEATURE [PartDesign::Mirrored] Mirror002
  MirrorPlane = -> XY_Plane003
  Refine = true
  Suppressed = false
  TransformMode = 0
FEATURE [PartDesign::PolarPattern] Polar_Pattern
  Angle = 360
  Axis = -> X_Axis003
  Mode = 0
  Occurrences = 12
  Offset = 120
  Refine = true
  SpacingPattern = [0]
  Spacings = [-1,-1,-1,-1,-1,-1,-1,-1,-1,-1,-1]
  Suppressed = false
  TransformMode = 0
FEATURE [PartDesign::MultiTransform] MultiTransform001
  BaseFeature = -> SubtractiveHelix002
  Originals = -> [SubtractiveHelix002]
  Refine = true
  Suppressed = false
  TransformMode = 0
  Transformations = -> [Mirror002,Polar_Pattern]
FEATURE [PartDesign::Body] Body003  label="A"
  AllowCompound = true
  Group = -> [Sketch010,Pad010,Sketch011,SubtractiveHelix,Chamfer005,Sketch016,Binder010,Binder008,Binder009,Binder011,SubtractiveHelix001,MultiTransform,Sketch025,Pad021,Chamfer003,Mirror,Mirror001,Sketch026,Pocket007,Sketch030,SubtractiveHelix002,MultiTransform001,Mirror002,Polar_Pattern]
  Origin = -> Origin006
  Tip = -> MultiTransform001
FEATURE [App::Part] Part  label="idée 1"
  Group = -> [Body,Body001,Body002]
  Origin = -> Origin012
FEATURE [App::Point] Origin013  label="Origine012"
  Role = Origin
FEATURE [App::Point] Origin015  label="Origine014"
  Role = Origin
FEATURE [App::Part] Part002  label="Idée 3"
  Origin = -> Origin016
FEATURE [App::Point] Origin017  label="Origine016"
  Role = Origin
FEATURE [Sketcher::SketchObject] Sketch031
  ArcFitTolerance = 1e-06
  AttachmentSupport = -> [Origin010]
  ExternalGeometry = -> [Binder005]
  ExternalTypes = [0,0,0]
  FullyConstrained = false
  MakeInternals = false
  MapMode = 5
  Placement = pos=(0,0,0) rot=(0.57735,0.57735,0.57735;2.0944rad)
  sketch-geometry (6):
    g0: LineSegment StartX=4.28092 StartY=2.46416 StartZ=0 EndX=4.28092 EndY=-2.46495 EndZ=0
    g1: LineSegment StartX=4.28092 StartY=-2.46495 StartZ=0 EndX=8.3666 EndY=-2.46495 EndZ=0
    g2: LineSegment StartX=8.3666 StartY=-2.46495 StartZ=0 EndX=8.3666 EndY=2.46416 EndZ=0
    g3: LineSegment StartX=8.3666 StartY=2.46416 StartZ=0 EndX=4.28092 EndY=2.46416 EndZ=0
    g4: ArcOfCircle [constr] CenterX=5.24597 CenterY=1.5 CenterZ=0 NormalX=0 NormalY=0 NormalZ=1 AngleXU=0 Radius=0.965348 StartAngle=1.62034 EndAngle=3.11649
    g5: ArcOfCircle [constr] CenterX=5.24597 CenterY=-1.5 CenterZ=0 NormalX=0 NormalY=0 NormalZ=1 AngleXU=0 Radius=0.965048 StartAngle=3.14464 EndAngle=4.7269
  constraints (16):
    c: Coincident(g0,g1)
    c: Coincident(g1,g2)
    c: Coincident(g2,g3)
    c: Coincident(g3,g0)
    c: Vertical(g0)
    c: Vertical(g2)
    c: Horizontal(g1)
    c: Horizontal(g3)
    c: Coincident(g4,g-4)
    c: PointOnObject(g4,g3)
    c: PointOnObject(g4,g0)
    c: Coincident(g5,g-5)
    c: PointOnObject(g5,g0)
    c: PointOnObject(g5,g1)
    c: Vertical(g-3,g2)
    c: Tangent(g4,g4)
FEATURE [PartDesign::Pocket] Pocket012
  BaseFeature = -> Chamfer006
  Direction = (-1,0,0)
  Length = 5
  Length2 = 5
  Profile = -> Sketch031
  ReferenceAxis = -> Sketch031 [N_Axis]
  Refine = true
  Reversed = true
  SideType = 0
  Suppressed = false
  Type = 1
  Type2 = 0
FEATURE [Sketcher::SketchObject] Sketch028
  ArcFitTolerance = 1e-06
  AttachmentSupport = -> [Chamfer006]
  ExternalGeometry = -> [Pocket012]
  ExternalTypes = [0,0,0]
  FullyConstrained = true
  MakeInternals = false
  MapMode = 5
  Placement = pos=(39.5,0,0) rot=(0.57735,0.57735,0.57735;2.0944rad)
  sketch-geometry (4):
    g0: ArcOfCircle CenterX=0 CenterY=0 CenterZ=0 NormalX=0 NormalY=0 NormalZ=1 AngleXU=0 Radius=8.8 StartAngle=0.283813 EndAngle=5.99928
    g1: LineSegment StartX=7.40053 StartY=2.46416 StartZ=0 EndX=8.44795 EndY=2.46416 EndZ=0
    g2: LineSegment StartX=7.40027 StartY=-2.46495 StartZ=0 EndX=8.44772 EndY=-2.46495 EndZ=0
    g3: LineSegment [constr] StartX=7.40027 StartY=-2.46495 StartZ=0 EndX=8.34903 EndY=-2.78097 EndZ=0
  constraints (11):
    c: Horizontal(g1)
    c: Horizontal(g2)
    c: Coincident(g1,g0)
    c: Coincident(g2,g0)
    c: Coincident(g3,g2)
    c: PointOnObject(g3,g0)
    c: Distance(g3,g3) = 1
    c: PointOnObject(g0,g3)
    c: Coincident(g2,g-5)
    c: Coincident(g-3,g1)
    c: Coincident(g0,g-1)
FEATURE [PartDesign::Pad] Pad025
  BaseFeature = -> Pocket012
  Direction = (1,0,0)
  Length = 3
  Length2 = 10
  Profile = -> Sketch028
  ReferenceAxis = -> Sketch028 [N_Axis]
  Refine = true
  SideType = 0
  Suppressed = false
  Type = 0
  Type2 = 0
FEATURE [PartDesign::Pocket] Pocket011
  BaseFeature = -> Pad025
  Direction = (-1,-1e-16,1e-16)
  Length = 5
  Length2 = 5
  Profile = -> Sketch029
  ReferenceAxis = -> Sketch029 [N_Axis]
  Refine = true
  SideType = 0
  Suppressed = false
  Type = 1
  Type2 = 0
FEATURE [PartDesign::Chamfer] Chamfer007
  Angle = 45
  Base = -> Pocket011 [Face11]
  BaseFeature = -> Pocket011
  ChamferType = 0
  FlipDirection = false
  Refine = true
  Size = 0.7
  Size2 = 1
  SupportTransform = false
  Suppressed = false
  UseAllEdges = false
FEATURE [PartDesign::Pocket] Pocket010
  BaseFeature = -> Chamfer007
  Direction = (0,0.5,-0.866025)
  Length = 5
  Length2 = 5
  Profile = -> Sketch022
  ReferenceAxis = -> Sketch022 [N_Axis]
  Refine = true
  SideType = 0
  Suppressed = false
  Type = 1
  Type2 = 0
FEATURE [PartDesign::PolarPattern] PolarPattern001
  Angle = 360
  Axis = -> X_Axis005
  BaseFeature = -> Pocket010
  Mode = 0
  Occurrences = 3
  Offset = 120
  Originals = -> [Pocket010]
  Refine = true
  SpacingPattern = [0]
  Spacings = [-1,-1]
  Suppressed = false
  TransformMode = 0
FEATURE [PartDesign::SubShapeBinder] Binder012
  BindCopyOnChange = 0
  BindMode = 0
  ClaimChildren = false
  Context = -> Part001 [Body004.Binder012.]
  Fuse = false
  MakeFace = true
  OffsetFill = false
  OffsetIntersection = false
  OffsetJoinType = 0
  OffsetOpenResult = false
  PartialLoad = false
  Refine = true
  Relative = true
  Support = -> [Body003[MultiTransform001.Face175,MultiTransform001.Face176,MultiTransform001.Face174,MultiTransform001.Face177]]
  _Version = 2
FEATURE [PartDesign::Pad] Pad026
  BaseFeature = -> Chamfer002
  Direction = (10,0,0)
  Length = 10
  Length2 = 10
  Profile = -> Binder012
  Refine = true
  SideType = 0
  Suppressed = false
  Type = 0
  Type2 = 0
  UseCustomVector = true
FEATURE [PartDesign::Body] Body004  label="B"
  AllowCompound = true
  Group = -> [Binder004,Sketch013,Pad017,Sketch024,Pad020,Chamfer002,Binder012,Pad026]
  Origin = -> Origin008
  Tip = -> Pad026
FEATURE [PartDesign::Chamfer] Chamfer008
  Angle = 45
  Base = -> PolarPattern001 [Edge99,Edge95]
  BaseFeature = -> PolarPattern001
  ChamferType = 0
  FlipDirection = false
  Refine = true
  Size = 1
  Size2 = 1
  SupportTransform = false
  Suppressed = false
  UseAllEdges = false
FEATURE [PartDesign::Body] Body005  label="Axe001"
  AllowCompound = true
  Group = -> [Binder005,Binder006,Binder007,Sketch015,Sketch022,Sketch023,Pad023,Sketch027,Pad024,Chamfer006,Pocket012,Sketch028,Pad025,Pocket011,Chamfer007,Pocket010,Sketch029,PolarPattern001,Sketch031,Chamfer008]
  Origin = -> Origin010
  Tip = -> Chamfer008
FEATURE [App::Part] Part001  label="Idée 2"
  Group = -> [Body003,Body004,Body005]
  Origin = -> Origin014
